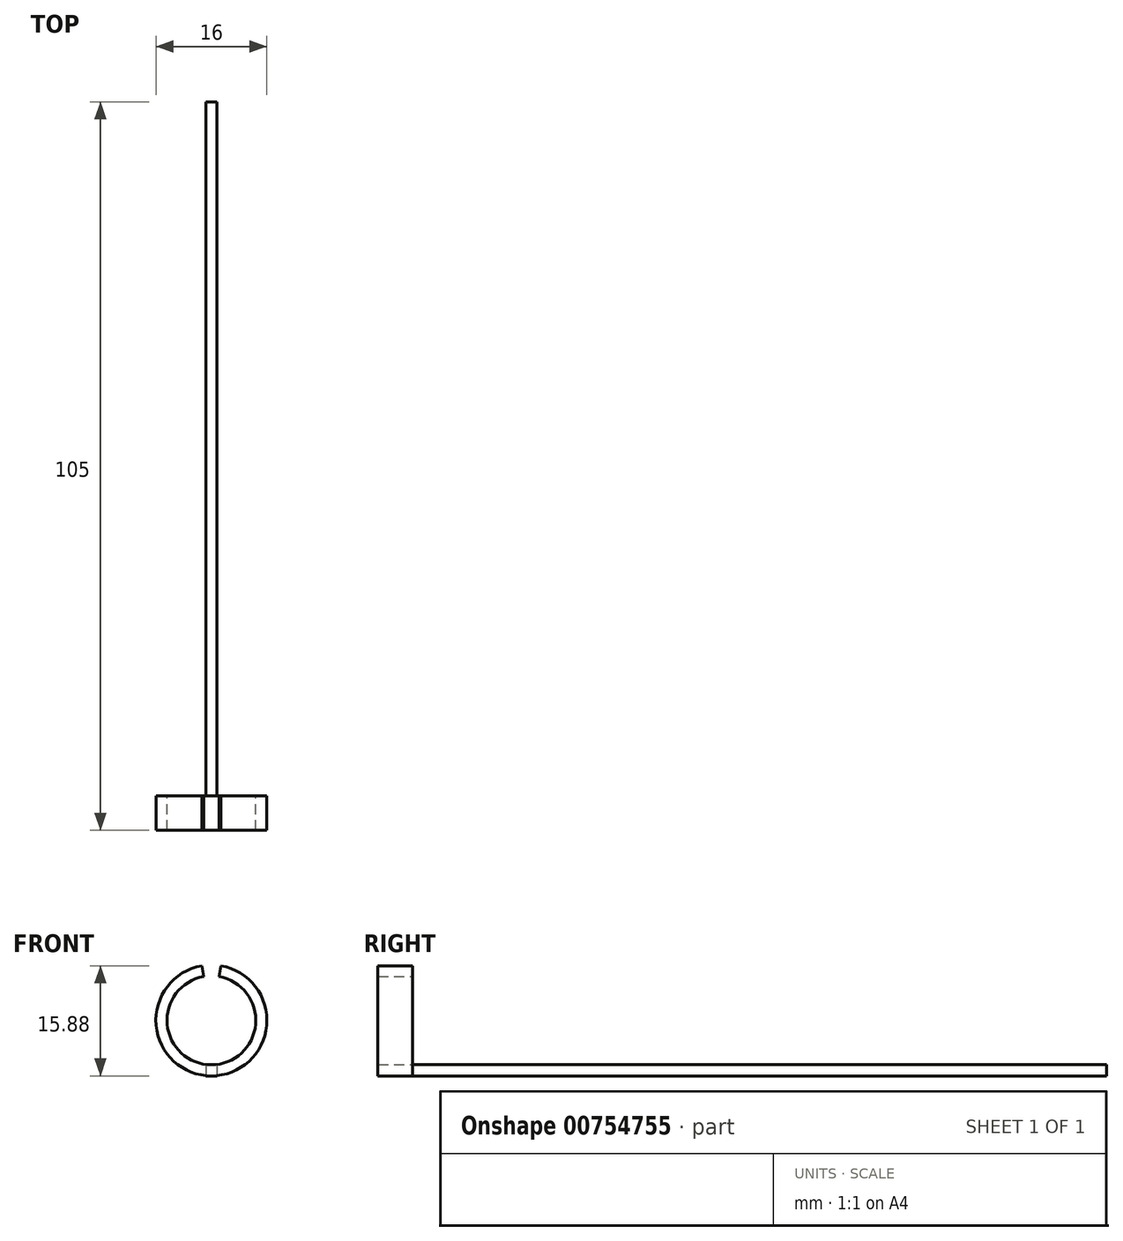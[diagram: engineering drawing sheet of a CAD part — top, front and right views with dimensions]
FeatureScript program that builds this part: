
annotation { "Feature Type Name" : "Feature", "Feature Type Description" : "" }
export const myFeature = defineFeature(function(context is Context, id is Id, definition is map)
    precondition{}
    {
        {
            var Q0;
            Q0=qCreatedBy(makeId("Top.planeOp"),FACE);
            var sketch = newSketch(context, id + "F0", { "sketchPlane" : qUnion([Q0])});
            skLineSegment(sketch, "E0.bottom", {"start": v(0.8, -50) * mm, "end": v(-0.8, -50) * mm});
            skLineSegment(sketch, "E0.top", {"start": v(0.8, 50) * mm, "end": v(-0.8, 50) * mm});
            skLineSegment(sketch, "E0.left", {"start": v(0.8, -50) * mm, "end": v(0.8, 50) * mm});
            skLineSegment(sketch, "E0.right", {"start": v(-0.8, -50) * mm, "end": v(-0.8, 50) * mm});
            skPoint(sketch, "E0.middle", {"position": v(0, 0) * mm});
            skSolve(sketch);
        }
        {
            var Q0;
            Q0=makeQuery(id+"F0.imprint","IMPRINT",FACE,{"disambiguationData":[TD([[makeQuery(id+"F0.imprint","IMPRINT",EDGE,{"derivedFrom":sQuery(id+"F0.wireOp",EDGE,"E0.bottom")}),-1.0]])]});
            extrude(context, id + "F1", {"entities" : qUnion([Q0]), "depth" : 1.6 * mm, "offsetDistance" : 25 * mm});
        }
        {
            var Q0;
            Q0=makeQuery(id+"F1.opExtrude","SWEPT_FACE",FACE,{"disambiguationData":[OSD([sQuery(id+"F0.wireOp",EDGE,"E0.bottom")])]});
            var sketch = newSketch(context, id + "F2", { "sketchPlane" : qUnion([Q0])});
            skPoint(sketch, "E1", {"position": v(0, 0.8) * mm});
            skPoint(sketch, "E2", {"position": v(0, 8) * mm});
            skCircle(sketch, "E3", {"center": v(0, 8) * mm, "radius": 8 * mm});
            skLineSegment(sketch, "E4", {"start": v(0, 8) * mm, "end": v(-1.71, 17.7) * mm, "construction": true});
            skLineSegment(sketch, "E5", {"start": v(0, 8) * mm, "end": v(1.7, 17.66) * mm, "construction": true});
            skCircle(sketch, "E6.0", {"center": v(0, 8) * mm, "radius": 6.4 * mm});
            skLineSegment(sketch, "E7", {"start": v(-1.11, 14.3) * mm, "end": v(-1.39, 15.88) * mm});
            skLineSegment(sketch, "E8", {"start": v(1.11, 14.3) * mm, "end": v(1.39, 15.88) * mm});
            skSolve(sketch);
        }
        {
            var Q0;
            {var subQ6=sQuery(id+"F2.wireOp",EDGE,"E7");Q0=makeQuery(id+"F2.imprint","IMPRINT",FACE,{"disambiguationData":[TD([[makeQuery(id+"F2.imprint","IMPRINT",EDGE,{"derivedFrom":subQ6}),1.0]])]});}
            var Q1;
            {var subQ6=sQuery(id+"F2.wireOp",EDGE,"E8");Q1=makeQuery(id+"F2.imprint","IMPRINT",FACE,{"disambiguationData":[TD([[makeQuery(id+"F2.imprint","IMPRINT",EDGE,{"derivedFrom":subQ6}),-1.0]])]});}
            var Q2;
            {var subQ0=sQuery(id+"F0.wireOp",EDGE,"E0.bottom");var subQ4=sQuery(id+"F2.wireOp",EDGE,"E3");var subQ9=makeQuery(id+"F2.imprint","INTERSECT",VERTEX,{"derivedFrom":[makeQuery(id+"F1.opExtrude","CAP_EDGE",EDGE,{"disambiguationData":[OSD([subQ0])],"isStart":true}),subQ4]});Q2=makeQuery(id+"F2.imprint","IMPRINT",FACE,{"disambiguationData":[TD([[makeQuery(id+"F2.imprint","IMPRINT",EDGE,{"disambiguationData":[TD([[subQ9,1.0]])],"derivedFrom":subQ4}),1.0]])]});}
            extrude(context, id + "F3", {"entities" : qUnion([Q0, Q1, Q2]), "operationType" : NewBodyOperationType.ADD, "depth" : 5 * mm, "offsetDistance" : 25 * mm});
        }
    });
